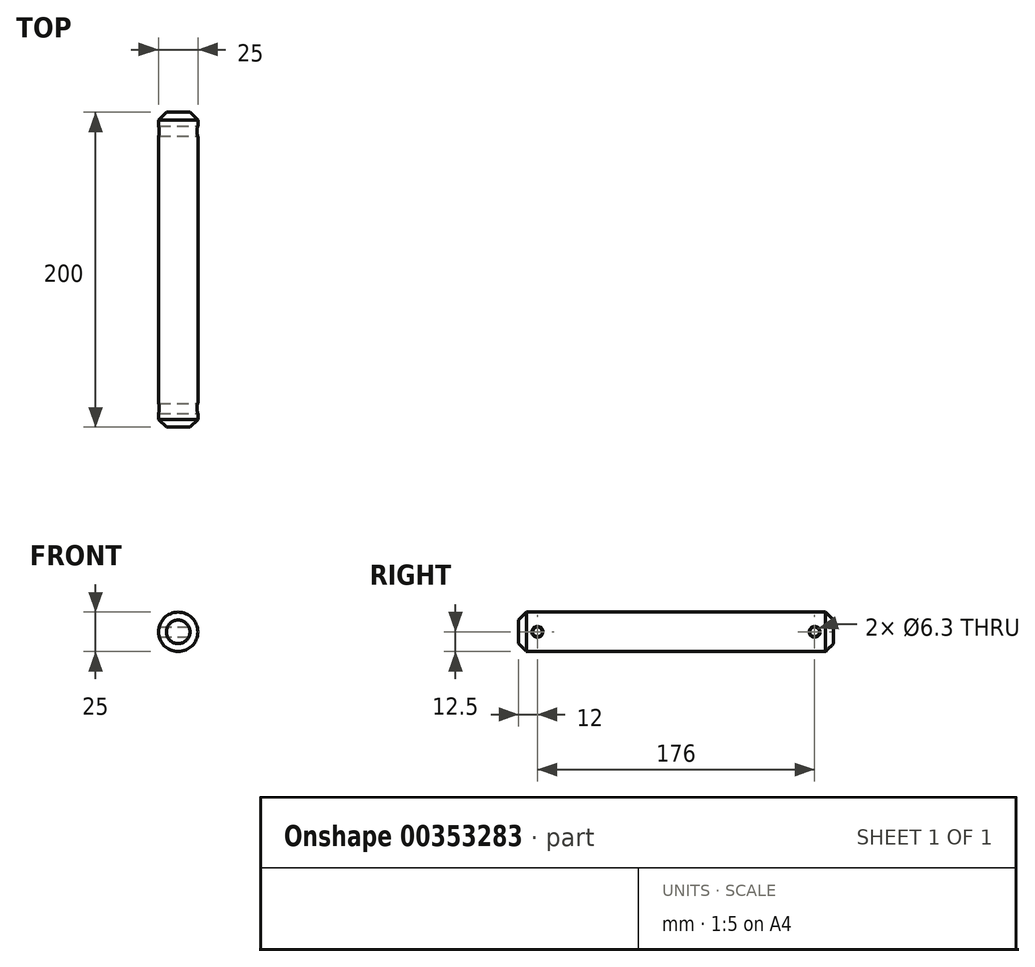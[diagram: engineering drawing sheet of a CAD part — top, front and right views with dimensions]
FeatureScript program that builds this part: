
annotation { "Feature Type Name" : "Feature", "Feature Type Description" : "" }
export const myFeature = defineFeature(function(context is Context, id is Id, definition is map)
    precondition{}
    {
        {
            var Q0;
            Q0=qCreatedBy(makeId("Front.planeOp"),FACE);
            var sketch = newSketch(context, id + "F0", { "sketchPlane" : qUnion([Q0])});
            skCircle(sketch, "E0", {"center": v(0, 0) * mm, "radius": 12.5 * mm});
            skSolve(sketch);
        }
        {
            var Q0;
            Q0=makeQuery(id+"F0.imprint","IMPRINT",FACE,{"disambiguationData":[TD([[makeQuery(id+"F0.imprint","IMPRINT",EDGE,{"derivedFrom":sQuery(id+"F0.wireOp",EDGE,"E0")}),1.0]])]});
            extrude(context, id + "F1", {"entities" : qUnion([Q0]), "depth" : 200 * mm});
        }
        {
            var Q0;
            Q0=qCreatedBy(makeId("Right.planeOp"),FACE);
            var sketch = newSketch(context, id + "F2", { "sketchPlane" : qUnion([Q0])});
            skCircle(sketch, "E1", {"center": v(-12, 0) * mm, "radius": 3.15 * mm});
            skCircle(sketch, "E2", {"center": v(-188, 0) * mm, "radius": 3.15 * mm});
            skSolve(sketch);
        }
        {
            var Q0;
            Q0 = qSketchRegion(id + "F2", true);
            extrude(context, id + "F3", {"entities" : qUnion([Q0]), "operationType" : NewBodyOperationType.REMOVE, "endBound" : BoundingType.SYMMETRIC, "oppositeDirection" : true, "depth" : 135.4 * mm});
        }
        {
            var Q0;
            Q0=makeQuery(id+"F1.opExtrude","CAP_EDGE",EDGE,{"disambiguationData":[OSD([sQuery(id+"F0.wireOp",EDGE,"E0")])],"isStart":true});
            var Q1;
            Q1=makeQuery(id+"F1.opExtrude","CAP_EDGE",EDGE,{"disambiguationData":[OSD([sQuery(id+"F0.wireOp",EDGE,"E0")])],"isStart":false});
            chamfer(context, id + "F4", {"entities" : qUnion([Q0, Q1]), "width" : 5 * mm, "tangentPropagation" : true});
        }
        {
            var Q0;
            Q0=makeQuery(id+"F3.boolean.opBoolean","INTERSECT",EDGE,{"disambiguationData":[OD(1.0)],"derivedFrom":[makeQuery(id+"F1.opExtrude","SWEPT_FACE",FACE,{"disambiguationData":[OSD([sQuery(id+"F0.wireOp",EDGE,"E0")])]}),makeQuery(id+"F3.opExtrude","SWEPT_FACE",FACE,{"disambiguationData":[OSD([sQuery(id+"F2.wireOp",EDGE,"E2")])]})]});
            var Q1;
            Q1=makeQuery(id+"F3.boolean.opBoolean","INTERSECT",EDGE,{"disambiguationData":[OD(0.0)],"derivedFrom":[makeQuery(id+"F1.opExtrude","SWEPT_FACE",FACE,{"disambiguationData":[OSD([sQuery(id+"F0.wireOp",EDGE,"E0")])]}),makeQuery(id+"F3.opExtrude","SWEPT_FACE",FACE,{"disambiguationData":[OSD([sQuery(id+"F2.wireOp",EDGE,"E2")])]})]});
            var Q2;
            Q2=makeQuery(id+"F3.boolean.opBoolean","INTERSECT",EDGE,{"disambiguationData":[OD(0.0)],"derivedFrom":[makeQuery(id+"F1.opExtrude","SWEPT_FACE",FACE,{"disambiguationData":[OSD([sQuery(id+"F0.wireOp",EDGE,"E0")])]}),makeQuery(id+"F3.opExtrude","SWEPT_FACE",FACE,{"disambiguationData":[OSD([sQuery(id+"F2.wireOp",EDGE,"E1")])]})]});
            var Q3;
            Q3=makeQuery(id+"F3.boolean.opBoolean","INTERSECT",EDGE,{"disambiguationData":[OD(1.0)],"derivedFrom":[makeQuery(id+"F1.opExtrude","SWEPT_FACE",FACE,{"disambiguationData":[OSD([sQuery(id+"F0.wireOp",EDGE,"E0")])]}),makeQuery(id+"F3.opExtrude","SWEPT_FACE",FACE,{"disambiguationData":[OSD([sQuery(id+"F2.wireOp",EDGE,"E1")])]})]});
            chamfer(context, id + "F5", {"entities" : qUnion([Q0, Q1, Q2, Q3]), "width" : .25 * mm, "tangentPropagation" : true});
        }
    });
